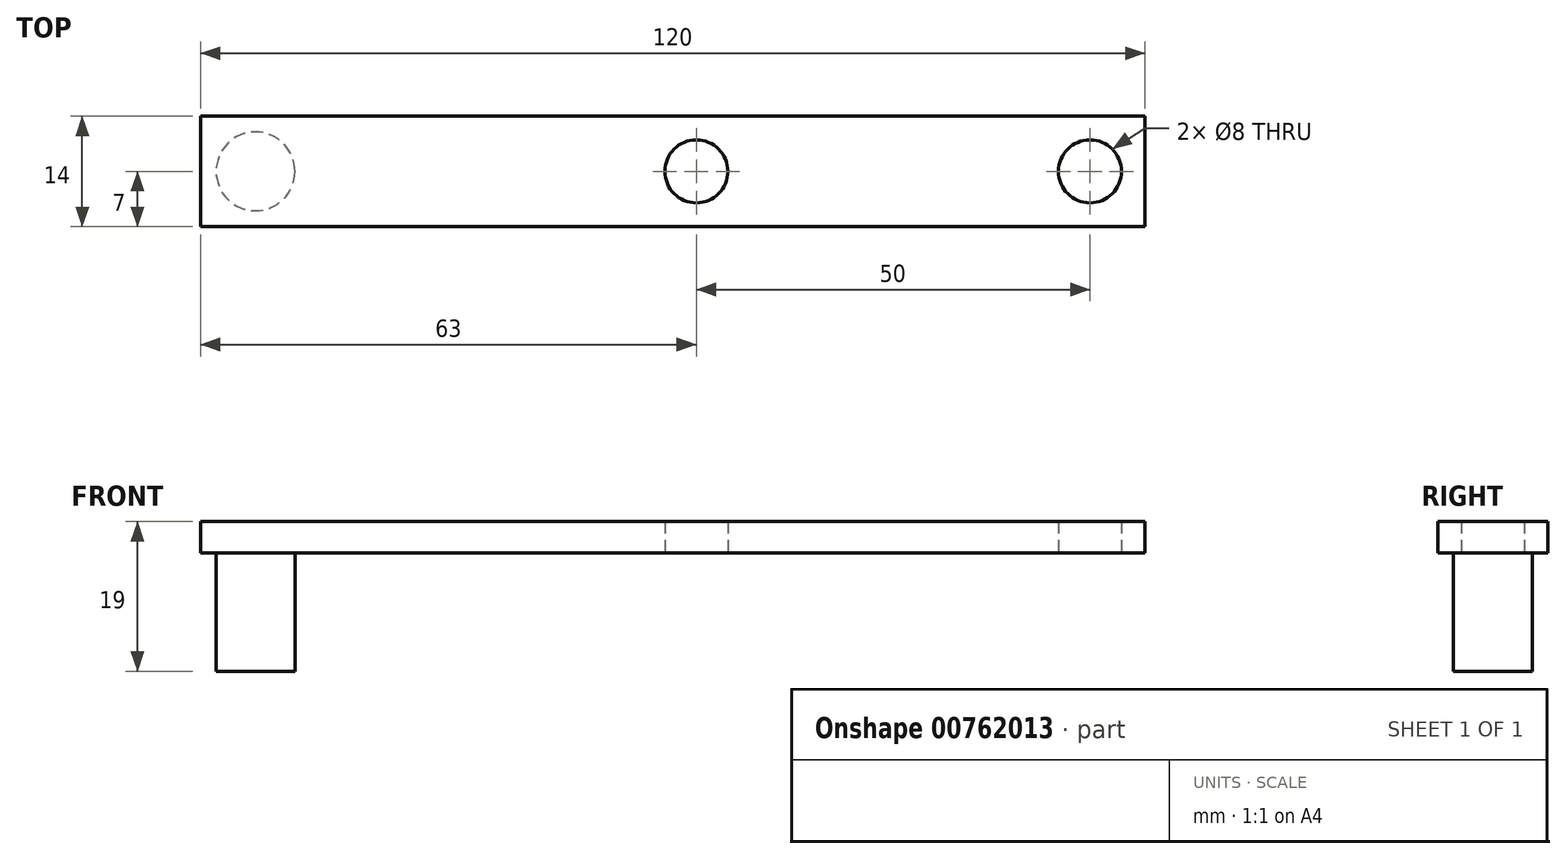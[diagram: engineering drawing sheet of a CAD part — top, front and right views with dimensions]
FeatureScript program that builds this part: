
annotation { "Feature Type Name" : "Feature", "Feature Type Description" : "" }
export const myFeature = defineFeature(function(context is Context, id is Id, definition is map)
    precondition{}
    {
        {
            var Q0;
            Q0=qCreatedBy(makeId("Top.planeOp"),FACE);
            var sketch = newSketch(context, id + "F0", { "sketchPlane" : qUnion([Q0])});
            skLineSegment(sketch, "E0.bottom", {"start": v(60, -7) * mm, "end": v(-60, -7) * mm});
            skLineSegment(sketch, "E0.top", {"start": v(60, 7) * mm, "end": v(-60, 7) * mm});
            skLineSegment(sketch, "E0.left", {"start": v(60, -7) * mm, "end": v(60, 7) * mm});
            skLineSegment(sketch, "E0.right", {"start": v(-60, -7) * mm, "end": v(-60, 7) * mm});
            skPoint(sketch, "E0.middle", {"position": v(0, 0) * mm});
            skCircle(sketch, "E1", {"center": v(53, 0) * mm, "radius": 4 * mm});
            skCircle(sketch, "E2", {"center": v(3, 0) * mm, "radius": 4 * mm});
            skCircle(sketch, "E3", {"center": v(-53, 0) * mm, "radius": 5 * mm});
            skSolve(sketch);
        }
        {
            var Q0;
            Q0 = qSketchRegion(id + "F0", true);
            var Q1;
            Q1=makeQuery(id+"F0.imprint","IMPRINT",FACE,{"disambiguationData":[TD([[makeQuery(id+"F0.imprint","IMPRINT",EDGE,{"derivedFrom":sQuery(id+"F0.wireOp",EDGE,"E3")}),1.0]])]});
            extrude(context, id + "F1", {"entities" : qUnion([Q0, Q1]), "depth" : 4 * mm, "offsetDistance" : 25 * mm});
        }
        {
            var Q0;
            Q0=makeQuery(id+"F0.imprint","IMPRINT",FACE,{"disambiguationData":[TD([[makeQuery(id+"F0.imprint","IMPRINT",EDGE,{"derivedFrom":sQuery(id+"F0.wireOp",EDGE,"E3")}),1.0]])]});
            extrude(context, id + "F2", {"entities" : qUnion([Q0]), "operationType" : NewBodyOperationType.ADD, "oppositeDirection" : true, "depth" : 15 * mm, "offsetDistance" : 25 * mm});
        }
    });
